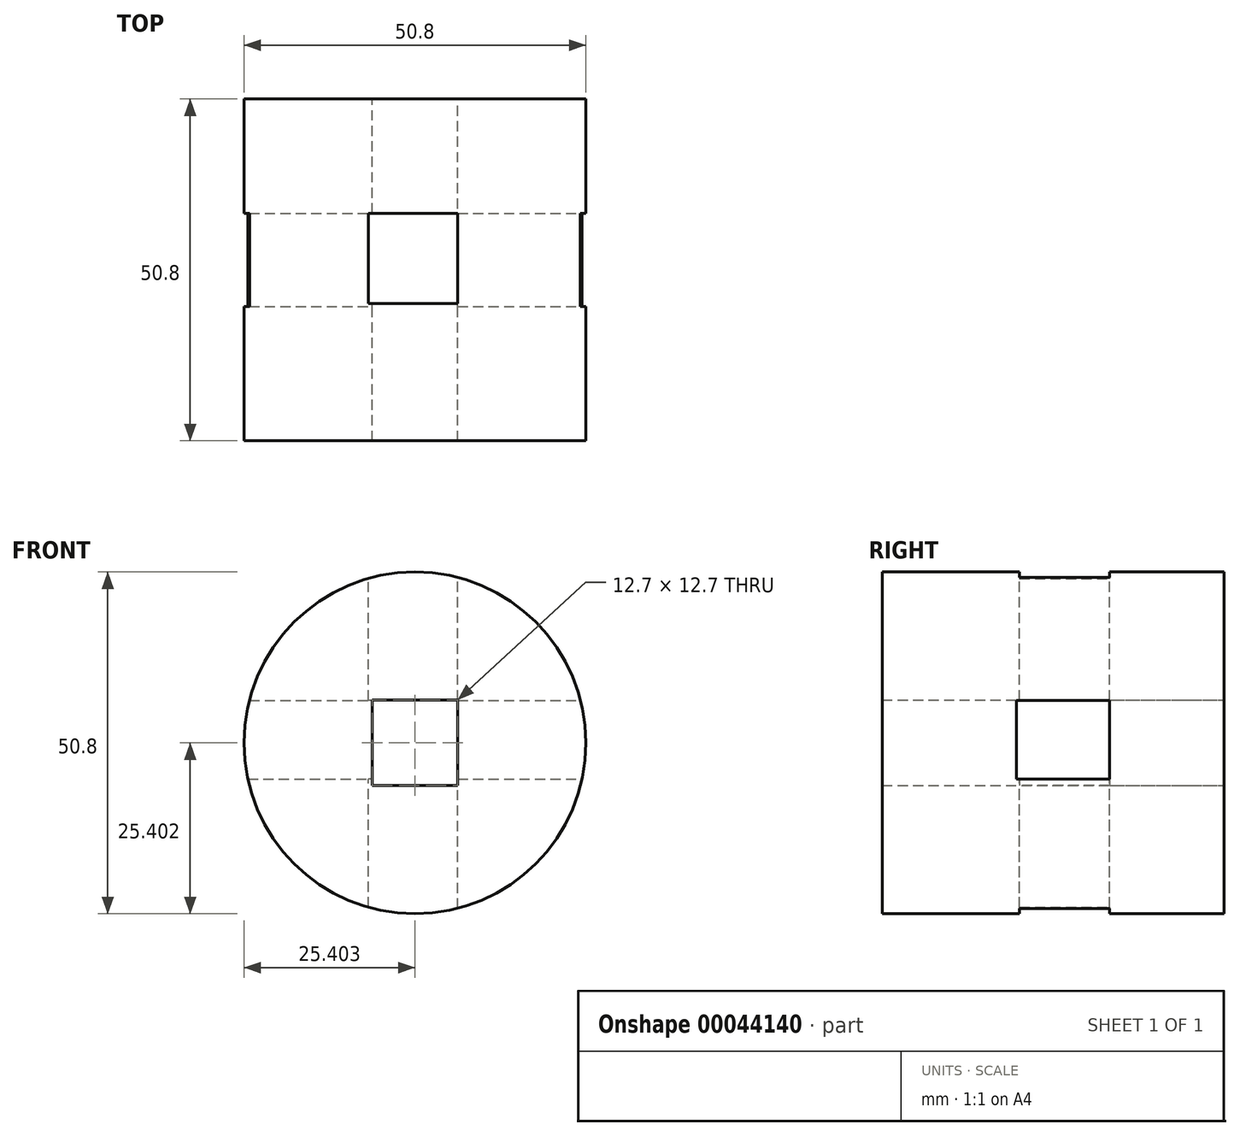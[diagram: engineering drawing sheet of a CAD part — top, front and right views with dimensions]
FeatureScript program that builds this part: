
annotation { "Feature Type Name" : "Feature", "Feature Type Description" : "" }
export const myFeature = defineFeature(function(context is Context, id is Id, definition is map)
    precondition{}
    {
        {
            var Q0;
            Q0=qCreatedBy(makeId("Front.planeOp"),FACE);
            var sketch = newSketch(context, id + "F0", { "sketchPlane" : qUnion([Q0])});
            skCircle(sketch, "E0", {"center": v(-6.33, 8.62) * mm, "radius": 25.4 * mm});
            skLineSegment(sketch, "E1.bottom", {"start": v(-12.68, 14.97) * mm, "end": v(0.02, 14.97) * mm});
            skLineSegment(sketch, "E1.top", {"start": v(-12.68, 2.27) * mm, "end": v(0.02, 2.27) * mm});
            skLineSegment(sketch, "E1.left", {"start": v(-12.68, 14.97) * mm, "end": v(-12.68, 2.27) * mm});
            skLineSegment(sketch, "E1.right", {"start": v(0.02, 14.97) * mm, "end": v(0.02, 2.27) * mm});
            skSolve(sketch);
        }
        {
            var Q0;
            Q0=makeQuery(id+"F0.imprint","IMPRINT",FACE,{"disambiguationData":[TD([[makeQuery(id+"F0.imprint","IMPRINT",EDGE,{"derivedFrom":sQuery(id+"F0.wireOp",EDGE,"E0")}),1.0]])]});
            var Q1;
            Q1=sQuery(id+"F0.wireOp",EDGE,"E0");
            extrude(context, id + "F1", {"entities" : qUnion([Q0]), "surfaceEntities" : qUnion([Q1]), "depth" : 50.8 * mm});
        }
        {
            var Q0;
            Q0=qCreatedBy(makeId("Right.planeOp"),FACE);
            var sketch = newSketch(context, id + "F2", { "sketchPlane" : qUnion([Q0])});
            skLineSegment(sketch, "E2.bottom", {"start": v(-30.86, 14.95) * mm, "end": v(-16.98, 14.95) * mm});
            skLineSegment(sketch, "E2.top", {"start": v(-30.86, 3.23) * mm, "end": v(-16.98, 3.23) * mm});
            skLineSegment(sketch, "E2.left", {"start": v(-30.86, 14.95) * mm, "end": v(-30.86, 3.23) * mm});
            skLineSegment(sketch, "E2.right", {"start": v(-16.98, 14.95) * mm, "end": v(-16.98, 3.23) * mm});
            skSolve(sketch);
        }
        {
            var Q0;
            Q0 = qSketchRegion(id + "F2", true);
            extrude(context, id + "F3", {"entities" : qUnion([Q0]), "operationType" : NewBodyOperationType.REMOVE, "endBound" : BoundingType.SYMMETRIC, "oppositeDirection" : true, "depth" : 101.6 * mm});
        }
        {
            var Q0;
            Q0=qCreatedBy(makeId("Top.planeOp"),FACE);
            var sketch = newSketch(context, id + "F4", { "sketchPlane" : qUnion([Q0])});
            skLineSegment(sketch, "E3.bottom", {"start": v(-13.28, -16.98) * mm, "end": v(0, -16.98) * mm});
            skLineSegment(sketch, "E3.top", {"start": v(-13.28, -30.38) * mm, "end": v(0, -30.38) * mm});
            skLineSegment(sketch, "E3.left", {"start": v(-13.28, -16.98) * mm, "end": v(-13.28, -30.38) * mm});
            skLineSegment(sketch, "E3.right", {"start": v(0, -16.98) * mm, "end": v(0, -30.38) * mm});
            skSolve(sketch);
        }
        {
            var Q0;
            Q0 = qSketchRegion(id + "F4", true);
            extrude(context, id + "F5", {"entities" : qUnion([Q0]), "operationType" : NewBodyOperationType.REMOVE, "endBound" : BoundingType.SYMMETRIC, "oppositeDirection" : true, "depth" : 101.6 * mm});
        }
    });
